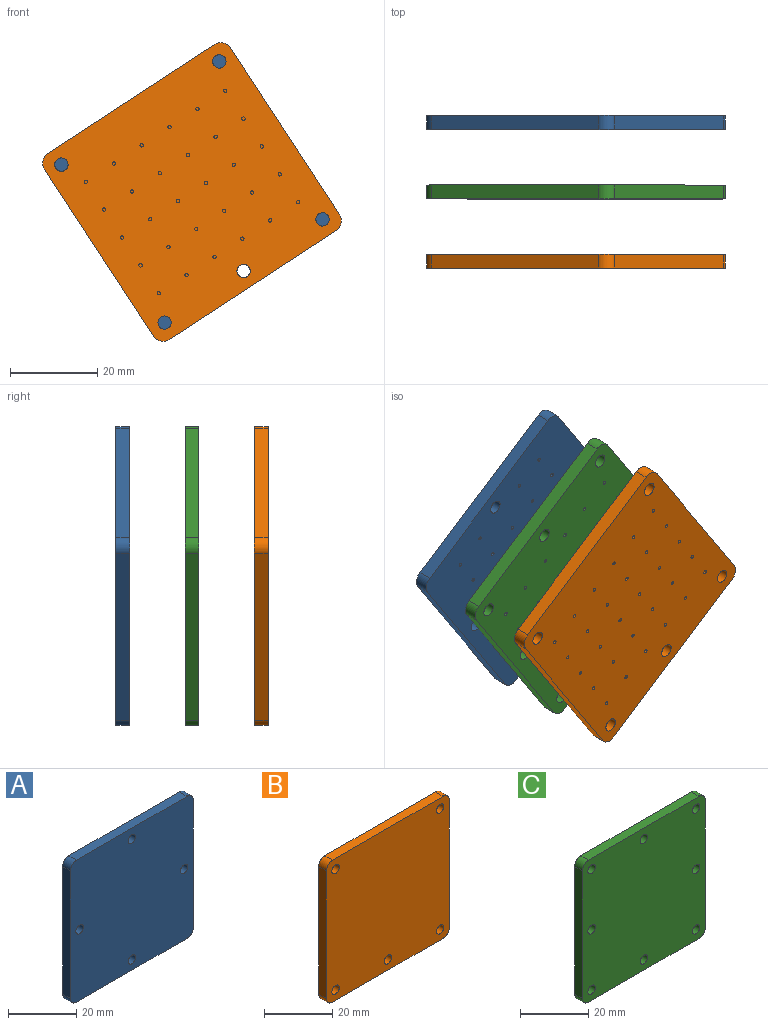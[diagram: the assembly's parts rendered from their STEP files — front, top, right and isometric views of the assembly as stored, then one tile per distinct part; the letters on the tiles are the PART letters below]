
ASSEMBLY  parts=3 mates=2
PART A: 70 faces, bbox 50.8x3.2x50.8 mm
  f0: plane 50.8x50.8mm, normal (0,1,0), area 2533.1mm2, adj f2,f3,f4,f5,f6,f7,f8,f9
  f1: plane 50.8x50.8mm, normal (0,-1,0), area 2545.9mm2, adj f2,f3,f4,f5,f6,f7,f8,f9
  f2: plane 45.72x3.18mm, normal (1,0,0), area 145.2mm2, adj f0,f1,f10,f13
  f3: plane 45.72x3.18mm, normal (0,0,1), area 145.2mm2, adj f0,f1,f10,f11
  f4: plane 45.72x3.18mm, normal (-1,0,0), area 145.2mm2, adj f0,f1,f11,f12
  f5: plane 45.72x3.18mm, normal (0,0,-1), area 145.2mm2, adj f0,f1,f12,f13
  f6: cylinder r=1.52mm len=3.18mm, axis (0,1,0), area 30.4mm2, adj f0,f1
  f7: cylinder r=1.52mm len=3.18mm, axis (0,1,0), area 30.4mm2, adj f0,f1
  f8: cylinder r=1.52mm len=3.18mm, axis (0,1,0), area 30.4mm2, adj f0,f1
  f9: cylinder r=1.52mm len=3.18mm, axis (0,1,0), area 30.4mm2, adj f0,f1
  f10: cylinder r=2.54mm len=3.18mm, axis (0,-1,0), area 12.7mm2, adj f0,f1,f2,f3
  f11: cylinder r=2.54mm len=3.18mm, axis (0,1,0), area 12.7mm2, adj f0,f1,f3,f4
  f12: cylinder r=2.54mm len=3.18mm, axis (0,-1,0), area 12.7mm2, adj f0,f1,f4,f5
  f13: cylinder r=2.54mm len=3.18mm, axis (0,1,0), area 12.7mm2, adj f0,f1,f2,f5
  f14: cylinder r=0.38mm len=1.27mm, axis (0,1,0), area 3mm2, adj f0,f15
  f15: plane 0.76x0.76mm, normal (0,1,0), area 0.5mm2, adj f14
  f16: cylinder r=0.38mm len=1.27mm, axis (0,1,0), area 3mm2, adj f0,f17
  f17: plane 0.76x0.76mm, normal (0,1,0), area 0.5mm2, adj f16
  f18: cylinder r=0.38mm len=1.27mm, axis (0,1,0), area 3mm2, adj f0,f19
  f19: plane 0.76x0.76mm, normal (0,1,0), area 0.5mm2, adj f18
  f20: cylinder r=0.38mm len=1.27mm, axis (0,1,0), area 3mm2, adj f0,f21
  f21: plane 0.76x0.76mm, normal (0,1,0), area 0.5mm2, adj f20
  f22: cylinder r=0.38mm len=1.27mm, axis (0,1,0), area 3mm2, adj f0,f23
  f23: plane 0.76x0.76mm, normal (0,1,0), area 0.5mm2, adj f22
  f24: cylinder r=0.38mm len=1.27mm, axis (0,1,0), area 3mm2, adj f0,f25
  f25: plane 0.76x0.76mm, normal (0,1,0), area 0.5mm2, adj f24
  f26: cylinder r=0.38mm len=1.27mm, axis (0,1,0), area 3mm2, adj f0,f27
  f27: plane 0.76x0.76mm, normal (0,1,0), area 0.5mm2, adj f26
  f28: cylinder r=0.38mm len=1.27mm, axis (0,1,0), area 3mm2, adj f0,f29
  f29: plane 0.76x0.76mm, normal (0,1,0), area 0.5mm2, adj f28
  f30: cylinder r=0.38mm len=1.27mm, axis (0,1,0), area 3mm2, adj f0,f31
  f31: plane 0.76x0.76mm, normal (0,1,0), area 0.5mm2, adj f30
  f32: cylinder r=0.38mm len=1.27mm, axis (0,1,0), area 3mm2, adj f0,f33
  f33: plane 0.76x0.76mm, normal (0,1,0), area 0.5mm2, adj f32
  f34: cylinder r=0.38mm len=1.27mm, axis (0,1,0), area 3mm2, adj f0,f35
  f35: plane 0.76x0.76mm, normal (0,1,0), area 0.5mm2, adj f34
  f36: cylinder r=0.38mm len=1.27mm, axis (0,1,0), area 3mm2, adj f0,f37
  f37: plane 0.76x0.76mm, normal (0,1,0), area 0.5mm2, adj f36
  f38: cylinder r=0.38mm len=1.27mm, axis (0,1,0), area 3mm2, adj f0,f39
  f39: plane 0.76x0.76mm, normal (0,1,0), area 0.5mm2, adj f38
  f40: cylinder r=0.38mm len=1.27mm, axis (0,1,0), area 3mm2, adj f0,f41
  f41: plane 0.76x0.76mm, normal (0,1,0), area 0.5mm2, adj f40
  f42: cylinder r=0.38mm len=1.27mm, axis (0,1,0), area 3mm2, adj f0,f43
  f43: plane 0.76x0.76mm, normal (0,1,0), area 0.5mm2, adj f42
  f44: cylinder r=0.38mm len=1.27mm, axis (0,1,0), area 3mm2, adj f0,f45
  f45: plane 0.76x0.76mm, normal (0,1,0), area 0.5mm2, adj f44
  f46: cylinder r=0.38mm len=1.27mm, axis (0,1,0), area 3mm2, adj f0,f47
  f47: plane 0.76x0.76mm, normal (0,1,0), area 0.5mm2, adj f46
  f48: cylinder r=0.38mm len=1.27mm, axis (0,1,0), area 3mm2, adj f0,f49
  f49: plane 0.76x0.76mm, normal (0,1,0), area 0.5mm2, adj f48
  f50: cylinder r=0.38mm len=1.27mm, axis (0,1,0), area 3mm2, adj f0,f51
  f51: plane 0.76x0.76mm, normal (0,1,0), area 0.5mm2, adj f50
  f52: cylinder r=0.38mm len=1.27mm, axis (0,1,0), area 3mm2, adj f0,f53
  f53: plane 0.76x0.76mm, normal (0,1,0), area 0.5mm2, adj f52
  f54: cylinder r=0.38mm len=1.27mm, axis (0,1,0), area 3mm2, adj f0,f55
  f55: plane 0.76x0.76mm, normal (0,1,0), area 0.5mm2, adj f54
  f56: cylinder r=0.38mm len=1.27mm, axis (0,1,0), area 3mm2, adj f0,f57
  f57: plane 0.76x0.76mm, normal (0,1,0), area 0.5mm2, adj f56
  f58: cylinder r=0.38mm len=1.27mm, axis (0,1,0), area 3mm2, adj f0,f59
  f59: plane 0.76x0.76mm, normal (0,1,0), area 0.5mm2, adj f58
  f60: cylinder r=0.38mm len=1.27mm, axis (0,1,0), area 3mm2, adj f0,f61
  f61: plane 0.76x0.76mm, normal (0,1,0), area 0.5mm2, adj f60
  f62: cylinder r=0.38mm len=1.27mm, axis (0,1,0), area 3mm2, adj f0,f63
  f63: plane 0.76x0.76mm, normal (0,1,0), area 0.5mm2, adj f62
  f64: cylinder r=0.38mm len=1.27mm, axis (0,1,0), area 3mm2, adj f0,f65
  f65: plane 0.76x0.76mm, normal (0,1,0), area 0.5mm2, adj f64
  f66: cylinder r=0.38mm len=1.27mm, axis (0,1,0), area 3mm2, adj f0,f67
  f67: plane 0.76x0.76mm, normal (0,1,0), area 0.5mm2, adj f66
  f68: cylinder r=0.38mm len=1.27mm, axis (0,1,0), area 3mm2, adj f0,f69
  f69: plane 0.76x0.76mm, normal (0,1,0), area 0.5mm2, adj f68
PART B: 75 faces, bbox 50.8x3.2x50.8 mm
  f0: plane 50.8x50.8mm, normal (0,1,0), area 2524.9mm2, adj f2,f3,f4,f5,f6,f7,f8,f9
  f1: plane 50.8x50.8mm, normal (0,-1,0), area 2538.6mm2, adj f2,f3,f4,f5,f6,f7,f8,f9
  f2: plane 45.72x3.18mm, normal (1,0,0), area 145.2mm2, adj f0,f1,f11,f14
  f3: plane 45.72x3.18mm, normal (0,0,1), area 145.2mm2, adj f0,f1,f11,f12
  f4: plane 45.72x3.18mm, normal (-1,0,0), area 145.2mm2, adj f0,f1,f12,f13
  f5: plane 45.72x3.18mm, normal (0,0,-1), area 145.2mm2, adj f0,f1,f13,f14
  f6: cylinder r=1.52mm len=3.18mm, axis (0,1,0), area 30.4mm2, adj f0,f1
  f7: cylinder r=1.52mm len=3.18mm, axis (0,1,0), area 30.4mm2, adj f0,f1
  f8: cylinder r=1.52mm len=3.18mm, axis (0,1,0), area 30.4mm2, adj f0,f1
  f9: cylinder r=1.52mm len=3.18mm, axis (0,1,0), area 30.4mm2, adj f0,f1
  f10: cylinder r=1.52mm len=3.18mm, axis (0,1,0), area 30.4mm2, adj f0,f1
  f11: cylinder r=2.54mm len=3.18mm, axis (0,-1,0), area 12.7mm2, adj f0,f1,f2,f3
  f12: cylinder r=2.54mm len=3.18mm, axis (0,1,0), area 12.7mm2, adj f0,f1,f3,f4
  f13: cylinder r=2.54mm len=3.18mm, axis (0,-1,0), area 12.7mm2, adj f0,f1,f4,f5
  f14: cylinder r=2.54mm len=3.18mm, axis (0,1,0), area 12.7mm2, adj f0,f1,f2,f5
  f15: cylinder r=0.38mm len=1.27mm, axis (0,1,0), area 3mm2, adj f0,f16
  f16: plane 0.76x0.76mm, normal (0,1,0), area 0.5mm2, adj f15
  f17: cylinder r=0.38mm len=1.27mm, axis (0,1,0), area 3mm2, adj f0,f18
  f18: plane 0.76x0.76mm, normal (0,1,0), area 0.5mm2, adj f17
  f19: cylinder r=0.38mm len=1.27mm, axis (0,1,0), area 3mm2, adj f0,f20
  f20: plane 0.76x0.76mm, normal (0,1,0), area 0.5mm2, adj f19
  f21: cylinder r=0.38mm len=1.27mm, axis (0,1,0), area 3mm2, adj f0,f22
  f22: plane 0.76x0.76mm, normal (0,1,0), area 0.5mm2, adj f21
  f23: cylinder r=0.38mm len=1.27mm, axis (0,1,0), area 3mm2, adj f0,f24
  f24: plane 0.76x0.76mm, normal (0,1,0), area 0.5mm2, adj f23
  f25: cylinder r=0.38mm len=1.27mm, axis (0,1,0), area 3mm2, adj f0,f26
  f26: plane 0.76x0.76mm, normal (0,1,0), area 0.5mm2, adj f25
  f27: cylinder r=0.38mm len=1.27mm, axis (0,1,0), area 3mm2, adj f0,f28
  f28: plane 0.76x0.76mm, normal (0,1,0), area 0.5mm2, adj f27
  f29: cylinder r=0.38mm len=1.27mm, axis (0,1,0), area 3mm2, adj f0,f30
  f30: plane 0.76x0.76mm, normal (0,1,0), area 0.5mm2, adj f29
  f31: cylinder r=0.38mm len=1.27mm, axis (0,1,0), area 3mm2, adj f0,f32
  f32: plane 0.76x0.76mm, normal (0,1,0), area 0.5mm2, adj f31
  f33: cylinder r=0.38mm len=1.27mm, axis (0,1,0), area 3mm2, adj f0,f34
  f34: plane 0.76x0.76mm, normal (0,1,0), area 0.5mm2, adj f33
  f35: cylinder r=0.38mm len=1.27mm, axis (0,1,0), area 3mm2, adj f0,f36
  f36: plane 0.76x0.76mm, normal (0,1,0), area 0.5mm2, adj f35
  f37: cylinder r=0.38mm len=1.27mm, axis (0,1,0), area 3mm2, adj f0,f38
  f38: plane 0.76x0.76mm, normal (0,1,0), area 0.5mm2, adj f37
  f39: cylinder r=0.38mm len=1.27mm, axis (0,1,0), area 3mm2, adj f0,f40
  f40: plane 0.76x0.76mm, normal (0,1,0), area 0.5mm2, adj f39
  f41: cylinder r=0.38mm len=1.27mm, axis (0,1,0), area 3mm2, adj f0,f42
  f42: plane 0.76x0.76mm, normal (0,1,0), area 0.5mm2, adj f41
  f43: cylinder r=0.38mm len=1.27mm, axis (0,1,0), area 3mm2, adj f0,f44
  f44: plane 0.76x0.76mm, normal (0,1,0), area 0.5mm2, adj f43
  f45: cylinder r=0.38mm len=1.27mm, axis (0,1,0), area 3mm2, adj f0,f46
  f46: plane 0.76x0.76mm, normal (0,1,0), area 0.5mm2, adj f45
  f47: cylinder r=0.38mm len=1.27mm, axis (0,1,0), area 3mm2, adj f0,f48
  f48: plane 0.76x0.76mm, normal (0,1,0), area 0.5mm2, adj f47
  f49: cylinder r=0.38mm len=1.27mm, axis (0,1,0), area 3mm2, adj f0,f50
  f50: plane 0.76x0.76mm, normal (0,1,0), area 0.5mm2, adj f49
  f51: cylinder r=0.38mm len=1.27mm, axis (0,1,0), area 3mm2, adj f0,f52
  f52: plane 0.76x0.76mm, normal (0,1,0), area 0.5mm2, adj f51
  f53: cylinder r=0.38mm len=1.27mm, axis (0,1,0), area 3mm2, adj f0,f54
  f54: plane 0.76x0.76mm, normal (0,1,0), area 0.5mm2, adj f53
  f55: cylinder r=0.38mm len=1.27mm, axis (0,1,0), area 3mm2, adj f0,f56
  f56: plane 0.76x0.76mm, normal (0,1,0), area 0.5mm2, adj f55
  f57: cylinder r=0.38mm len=1.27mm, axis (0,1,0), area 3mm2, adj f0,f58
  f58: plane 0.76x0.76mm, normal (0,1,0), area 0.5mm2, adj f57
  f59: cylinder r=0.38mm len=1.27mm, axis (0,1,0), area 3mm2, adj f0,f60
  f60: plane 0.76x0.76mm, normal (0,1,0), area 0.5mm2, adj f59
  f61: cylinder r=0.38mm len=1.27mm, axis (0,1,0), area 3mm2, adj f0,f62
  f62: plane 0.76x0.76mm, normal (0,1,0), area 0.5mm2, adj f61
  f63: cylinder r=0.38mm len=1.27mm, axis (0,1,0), area 3mm2, adj f0,f64
  f64: plane 0.76x0.76mm, normal (0,1,0), area 0.5mm2, adj f63
  f65: cylinder r=0.38mm len=1.27mm, axis (0,1,0), area 3mm2, adj f0,f66
  f66: plane 0.76x0.76mm, normal (0,1,0), area 0.5mm2, adj f65
  f67: cylinder r=0.38mm len=1.27mm, axis (0,1,0), area 3mm2, adj f0,f68
  f68: plane 0.76x0.76mm, normal (0,1,0), area 0.5mm2, adj f67
  f69: cylinder r=0.38mm len=1.27mm, axis (0,1,0), area 3mm2, adj f0,f70
  f70: plane 0.76x0.76mm, normal (0,1,0), area 0.5mm2, adj f69
  f71: cylinder r=0.38mm len=1.27mm, axis (0,1,0), area 3mm2, adj f0,f72
  f72: plane 0.76x0.76mm, normal (0,1,0), area 0.5mm2, adj f71
  f73: cylinder r=0.38mm len=1.27mm, axis (0,1,0), area 3mm2, adj f0,f74
  f74: plane 0.76x0.76mm, normal (0,1,0), area 0.5mm2, adj f73
PART C: 78 faces, bbox 50.8x3.2x50.8 mm
  f0: plane 50.8x50.8mm, normal (0,1,0), area 2503mm2, adj f2,f3,f4,f5,f6,f7,f8,f9
  f1: plane 50.8x50.8mm, normal (0,-1,0), area 2516.7mm2, adj f2,f3,f4,f5,f6,f7,f8,f9
  f2: plane 45.72x3.18mm, normal (1,0,0), area 145.2mm2, adj f0,f1,f10,f13
  f3: plane 45.72x3.18mm, normal (0,0,1), area 145.2mm2, adj f0,f1,f10,f11
  f4: plane 45.72x3.18mm, normal (-1,0,0), area 145.2mm2, adj f0,f1,f11,f12
  f5: plane 45.72x3.18mm, normal (0,0,-1), area 145.2mm2, adj f0,f1,f12,f13
  f6: cylinder r=1.52mm len=3.18mm, axis (0,1,0), area 30.4mm2, adj f0,f1
  f7: cylinder r=1.52mm len=3.18mm, axis (0,1,0), area 30.4mm2, adj f0,f1
  f8: cylinder r=1.52mm len=3.18mm, axis (0,1,0), area 30.4mm2, adj f0,f1
  f9: cylinder r=1.52mm len=3.18mm, axis (0,1,0), area 30.4mm2, adj f0,f1
  f10: cylinder r=2.54mm len=3.18mm, axis (0,-1,0), area 12.7mm2, adj f0,f1,f2,f3
  f11: cylinder r=2.54mm len=3.18mm, axis (0,1,0), area 12.7mm2, adj f0,f1,f3,f4
  f12: cylinder r=2.54mm len=3.18mm, axis (0,-1,0), area 12.7mm2, adj f0,f1,f4,f5
  f13: cylinder r=2.54mm len=3.18mm, axis (0,1,0), area 12.7mm2, adj f0,f1,f2,f5
  f14: cylinder r=0.38mm len=1.27mm, axis (0,1,0), area 3mm2, adj f0,f15
  f15: plane 0.76x0.76mm, normal (0,1,0), area 0.5mm2, adj f14
  f16: cylinder r=0.38mm len=1.27mm, axis (0,1,0), area 3mm2, adj f0,f17
  f17: plane 0.76x0.76mm, normal (0,1,0), area 0.5mm2, adj f16
  f18: cylinder r=0.38mm len=1.27mm, axis (0,1,0), area 3mm2, adj f0,f19
  f19: plane 0.76x0.76mm, normal (0,1,0), area 0.5mm2, adj f18
  f20: cylinder r=0.38mm len=1.27mm, axis (0,1,0), area 3mm2, adj f0,f21
  f21: plane 0.76x0.76mm, normal (0,1,0), area 0.5mm2, adj f20
  f22: cylinder r=0.38mm len=1.27mm, axis (0,1,0), area 3mm2, adj f0,f23
  f23: plane 0.76x0.76mm, normal (0,1,0), area 0.5mm2, adj f22
  f24: cylinder r=0.38mm len=1.27mm, axis (0,1,0), area 3mm2, adj f0,f25
  f25: plane 0.76x0.76mm, normal (0,1,0), area 0.5mm2, adj f24
  f26: cylinder r=0.38mm len=1.27mm, axis (0,1,0), area 3mm2, adj f0,f27
  f27: plane 0.76x0.76mm, normal (0,1,0), area 0.5mm2, adj f26
  f28: cylinder r=0.38mm len=1.27mm, axis (0,1,0), area 3mm2, adj f0,f29
  f29: plane 0.76x0.76mm, normal (0,1,0), area 0.5mm2, adj f28
  f30: cylinder r=0.38mm len=1.27mm, axis (0,1,0), area 3mm2, adj f0,f31
  f31: plane 0.76x0.76mm, normal (0,1,0), area 0.5mm2, adj f30
  f32: cylinder r=0.38mm len=1.27mm, axis (0,1,0), area 3mm2, adj f0,f33
  f33: plane 0.76x0.76mm, normal (0,1,0), area 0.5mm2, adj f32
  f34: cylinder r=0.38mm len=1.27mm, axis (0,1,0), area 3mm2, adj f0,f35
  f35: plane 0.76x0.76mm, normal (0,1,0), area 0.5mm2, adj f34
  f36: cylinder r=0.38mm len=1.27mm, axis (0,1,0), area 3mm2, adj f0,f37
  f37: plane 0.76x0.76mm, normal (0,1,0), area 0.5mm2, adj f36
  f38: cylinder r=0.38mm len=1.27mm, axis (0,1,0), area 3mm2, adj f0,f39
  f39: plane 0.76x0.76mm, normal (0,1,0), area 0.5mm2, adj f38
  f40: cylinder r=0.38mm len=1.27mm, axis (0,1,0), area 3mm2, adj f0,f41
  f41: plane 0.76x0.76mm, normal (0,1,0), area 0.5mm2, adj f40
  f42: cylinder r=0.38mm len=1.27mm, axis (0,1,0), area 3mm2, adj f0,f43
  f43: plane 0.76x0.76mm, normal (0,1,0), area 0.5mm2, adj f42
  f44: cylinder r=0.38mm len=1.27mm, axis (0,1,0), area 3mm2, adj f0,f45
  f45: plane 0.76x0.76mm, normal (0,1,0), area 0.5mm2, adj f44
  f46: cylinder r=0.38mm len=1.27mm, axis (0,1,0), area 3mm2, adj f0,f47
  f47: plane 0.76x0.76mm, normal (0,1,0), area 0.5mm2, adj f46
  f48: cylinder r=0.38mm len=1.27mm, axis (0,1,0), area 3mm2, adj f0,f49
  f49: plane 0.76x0.76mm, normal (0,1,0), area 0.5mm2, adj f48
  f50: cylinder r=0.38mm len=1.27mm, axis (0,1,0), area 3mm2, adj f0,f51
  f51: plane 0.76x0.76mm, normal (0,1,0), area 0.5mm2, adj f50
  f52: cylinder r=0.38mm len=1.27mm, axis (0,1,0), area 3mm2, adj f0,f53
  f53: plane 0.76x0.76mm, normal (0,1,0), area 0.5mm2, adj f52
  f54: cylinder r=0.38mm len=1.27mm, axis (0,1,0), area 3mm2, adj f0,f55
  f55: plane 0.76x0.76mm, normal (0,1,0), area 0.5mm2, adj f54
  f56: cylinder r=0.38mm len=1.27mm, axis (0,1,0), area 3mm2, adj f0,f57
  f57: plane 0.76x0.76mm, normal (0,1,0), area 0.5mm2, adj f56
  f58: cylinder r=0.38mm len=1.27mm, axis (0,1,0), area 3mm2, adj f0,f59
  f59: plane 0.76x0.76mm, normal (0,1,0), area 0.5mm2, adj f58
  f60: cylinder r=0.38mm len=1.27mm, axis (0,1,0), area 3mm2, adj f0,f61
  f61: plane 0.76x0.76mm, normal (0,1,0), area 0.5mm2, adj f60
  f62: cylinder r=0.38mm len=1.27mm, axis (0,1,0), area 3mm2, adj f0,f63
  f63: plane 0.76x0.76mm, normal (0,1,0), area 0.5mm2, adj f62
  f64: cylinder r=0.38mm len=1.27mm, axis (0,1,0), area 3mm2, adj f0,f65
  f65: plane 0.76x0.76mm, normal (0,1,0), area 0.5mm2, adj f64
  f66: cylinder r=0.38mm len=1.27mm, axis (0,1,0), area 3mm2, adj f0,f67
  f67: plane 0.76x0.76mm, normal (0,1,0), area 0.5mm2, adj f66
  f68: cylinder r=0.38mm len=1.27mm, axis (0,1,0), area 3mm2, adj f0,f69
  f69: plane 0.76x0.76mm, normal (0,1,0), area 0.5mm2, adj f68
  f70: cylinder r=0.38mm len=1.27mm, axis (0,1,0), area 3mm2, adj f0,f71
  f71: plane 0.76x0.76mm, normal (0,1,0), area 0.5mm2, adj f70
  f72: cylinder r=0.38mm len=1.27mm, axis (0,1,0), area 3mm2, adj f0,f73
  f73: plane 0.76x0.76mm, normal (0,1,0), area 0.5mm2, adj f72
  f74: cylinder r=1.52mm len=3.18mm, axis (0,1,0), area 30.4mm2, adj f0,f1
  f75: cylinder r=1.52mm len=3.18mm, axis (0,1,0), area 30.4mm2, adj f0,f1
  f76: cylinder r=1.52mm len=3.18mm, axis (0,1,0), area 30.4mm2, adj f0,f1
  f77: cylinder r=1.52mm len=3.18mm, axis (0,1,0), area 30.4mm2, adj f0,f1
PLACE A rot(axis=(0.88,0,-0.48),180deg) t=(4.03,-6.91,-26.49)mm
PLACE B rot(axis=(0.29,0,-0.96),180deg) t=(4.03,-38.66,-26.49)mm
PLACE C rot(axis=(0.29,0,-0.96),180deg) t=(4.03,-22.78,-26.49)mm
MATE fastened B.f55 <-> C.f54  axis (0,-1,0) through (11.65,-38.66,-3.31)mm
MATE fastened A.f6 <-> C.f76  axis (0,-1,0) through (-7.78,-6.91,-8.41)mm
